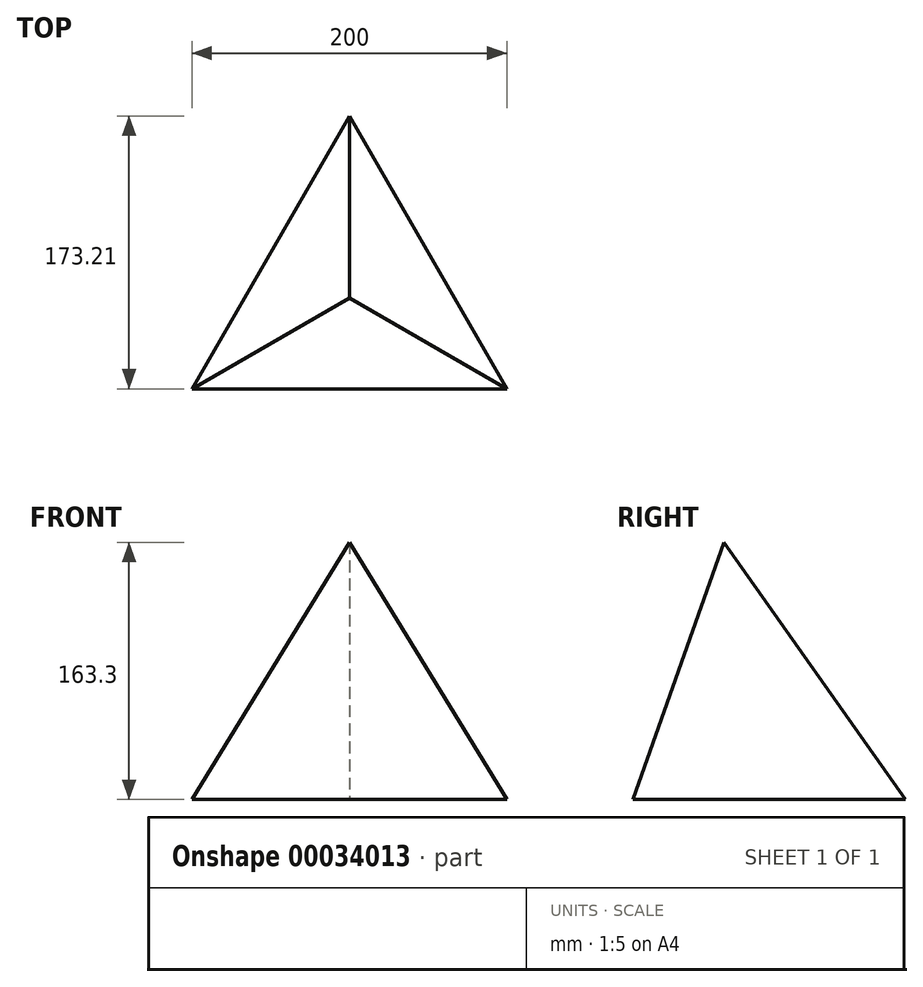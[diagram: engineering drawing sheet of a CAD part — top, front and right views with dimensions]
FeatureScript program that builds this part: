
annotation { "Feature Type Name" : "Feature", "Feature Type Description" : "" }
export const myFeature = defineFeature(function(context is Context, id is Id, definition is map)
    precondition{}
    {
        {
            var Q0;
            Q0=qCreatedBy(makeId("Top.planeOp"),FACE);
            var sketch = newSketch(context, id + "F0", { "sketchPlane" : qUnion([Q0])});
            skLineSegment(sketch, "E0", {"start": v(0, 115.47) * mm, "end": v(100, -57.74) * mm});
            skLineSegment(sketch, "E1", {"start": v(100, -57.74) * mm, "end": v(-100, -57.74) * mm});
            skLineSegment(sketch, "E2", {"start": v(-100, -57.74) * mm, "end": v(0, 115.47) * mm});
            skLineSegment(sketch, "E3", {"start": v(0, 115.47) * mm, "end": v(0, 0) * mm});
            skLineSegment(sketch, "E4", {"start": v(-100, -57.74) * mm, "end": v(0, 0) * mm});
            skLineSegment(sketch, "E5", {"start": v(0, 0) * mm, "end": v(100, -57.74) * mm});
            skPoint(sketch, "E6.orphan", {"position": v(0, -57.74) * mm});
            skLineSegment(sketch, "E7", {"start": v(0, 115.47) * mm, "end": v(0, -57.74) * mm, "construction": true});
            skSolve(sketch);
        }
        {
            assignVariable(context, id + "F1", {"name" : "Angle", "anyValue" : 70.53});
        }
        {
            var Q0;
            Q0 = qSketchRegion(id + "F0", true);
            extrude(context, id + "F2", {"entities" : qUnion([Q0]), "depth" : 1000 * mm, "hasDraft" : true, "draftAngle" : (90 - getVariable(context, 'Angle')) * degree, "draftPullDirection" : true});
        }
    });
